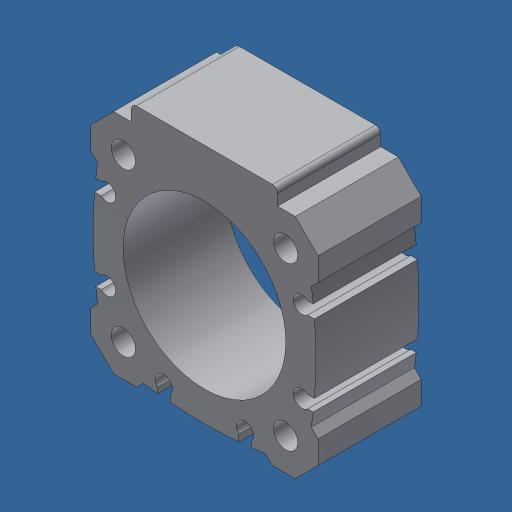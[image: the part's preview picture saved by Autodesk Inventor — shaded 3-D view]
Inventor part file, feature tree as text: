
AUTODESK INVENTOR PART (.ipt)
format: ipt  version: 2024.3 (Build 283343000, 343)  size: 246,784 bytes
history: native  units: mm (DEFAULTED — no unit token found)
features: other x1, extrude x1, sketch x1
ambient origin geometry x8: Origin, YZ Plane, XZ Plane, XY Plane, X Axis, Y Axis, Z Axis, Center Point
bodies: Body1 (feature_tree)
feature tree (3):
  other  "Finish - None"
  extrude  "PHD, 40MM"  Depth=25.4mm
  sketch  "Sketch1"  dims[d0=69.479mm d1=193.924mm d2=69.479mm d3=193.924mm d4=32.004mm d5=18.034mm d6=2.54mm d7=27.991mm d8=135.0deg d9=28.0mm d10=4.363mm d11=16.697mm d12=135.0deg d13=10.008mm d14=24.003mm d15=4.242mm d16=11.545mm d17=8.472mm d18=96.962mm d19=10.008mm d20=4.242mm d21=8.472mm d22=11.545mm d23=96.962mm d24=15.011mm d25=96.962mm d26=45.0deg d27=28.0mm d28=22.393mm d29=135.0deg d30=22.397mm d31=16.693mm d32=135.0deg d33=96.962mm d34=10.008mm d35=24.003mm d36=4.242mm d37=11.545mm d38=11.545mm d39=8.472mm d40=96.962mm d41=96.962mm d42=40.132mm d43=20.0mm d44=20.003mm d45=6.0mm d46=20.003mm d47=6.0mm d48=25.4mm d49=0.0mm]
